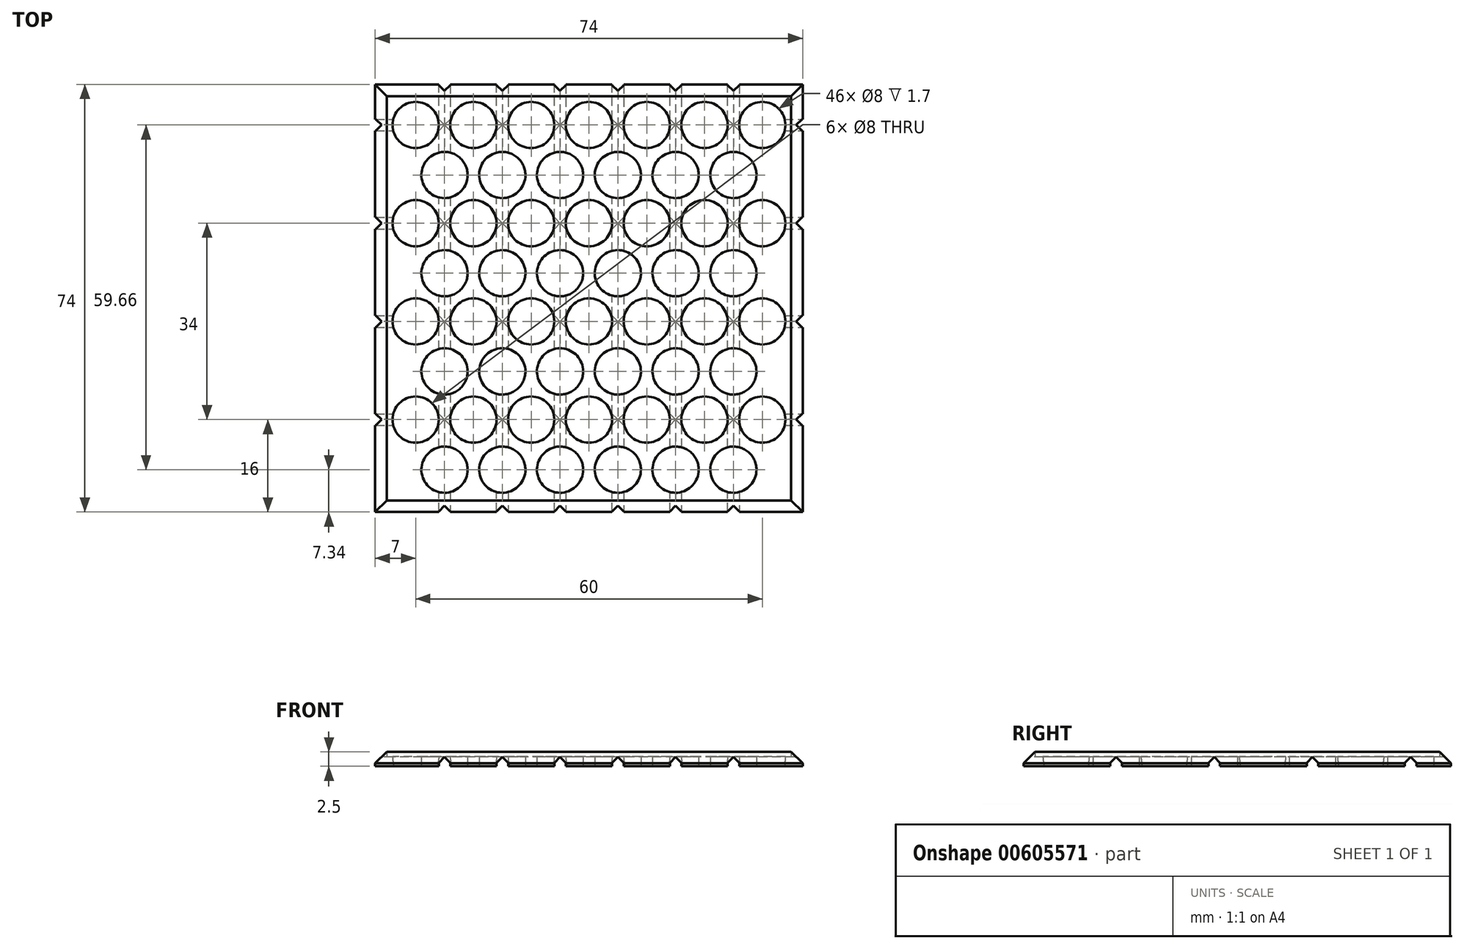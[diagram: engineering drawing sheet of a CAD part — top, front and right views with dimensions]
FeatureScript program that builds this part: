
annotation { "Feature Type Name" : "Feature", "Feature Type Description" : "" }
export const myFeature = defineFeature(function(context is Context, id is Id, definition is map)
    precondition{}
    {
        {
            var Q0;
            Q0=qCreatedBy(makeId("Top.planeOp"),FACE);
            var sketch = newSketch(context, id + "F0", { "sketchPlane" : qUnion([Q0])});
            skLineSegment(sketch, "E0.bottom", {"start": v(0, 0) * mm, "end": v(70, 0) * mm});
            skLineSegment(sketch, "E0.top", {"start": v(0, 70) * mm, "end": v(70, 70) * mm});
            skLineSegment(sketch, "E0.left", {"start": v(0, 0) * mm, "end": v(0, 70) * mm});
            skLineSegment(sketch, "E0.right", {"start": v(70, 0) * mm, "end": v(70, 70) * mm});
            skLineSegment(sketch, "E1.0", {"start": v(-2, 72) * mm, "end": v(72, 72) * mm});
            skLineSegment(sketch, "E1.1", {"start": v(-2, -2) * mm, "end": v(-2, 72) * mm});
            skLineSegment(sketch, "E1.2", {"start": v(-2, -2) * mm, "end": v(72, -2) * mm});
            skLineSegment(sketch, "E1.3", {"start": v(72, -2) * mm, "end": v(72, 72) * mm});
            skSolve(sketch);
        }
        {
            var Q0;
            Q0=makeQuery(id+"F0.imprint","IMPRINT",FACE,{"disambiguationData":[TD([[makeQuery(id+"F0.imprint","IMPRINT",EDGE,{"derivedFrom":sQuery(id+"F0.wireOp",EDGE,"E0.bottom")}),-1.0]])]});
            extrude(context, id + "F1", {"entities" : qUnion([Q0]), "depth" : 2.5 * mm, "offsetDistance" : 25 * mm});
        }
        {
            var Q0;
            Q0=makeQuery(id+"F0.imprint","IMPRINT",FACE,{"disambiguationData":[TD([[makeQuery(id+"F0.imprint","IMPRINT",EDGE,{"derivedFrom":sQuery(id+"F0.wireOp",EDGE,"E0.bottom")}),1.0]])]});
            var Q1;
            Q1=makeQuery(id+"F0.imprint","IMPRINT",FACE,{"disambiguationData":[TD([[makeQuery(id+"F0.imprint","IMPRINT",EDGE,{"derivedFrom":sQuery(id+"F0.wireOp",EDGE,"E0.bottom")}),-1.0]])]});
            extrude(context, id + "F2", {"entities" : qUnion([Q0, Q1]), "operationType" : NewBodyOperationType.ADD, "depth" : 1.7 * mm, "offsetDistance" : 25 * mm});
        }
        {
            var Q0;
            Q0=qCreatedBy(makeId("Top.planeOp"),FACE);
            var sketch = newSketch(context, id + "F3", { "sketchPlane" : qUnion([Q0])});
            skLineSegment(sketch, "E2", {"start": v(9, -4) * mm, "end": v(9, 76) * mm});
            skLineSegment(sketch, "E3", {"start": v(9, 76) * mm, "end": v(11, 76) * mm});
            skLineSegment(sketch, "E4", {"start": v(11, 76) * mm, "end": v(11, -4) * mm});
            skLineSegment(sketch, "E5", {"start": v(11, -4) * mm, "end": v(9, -4) * mm});
            skLineSegment(sketch, "E6.1.0.0", {"start": v(21, -4) * mm, "end": v(19, -4) * mm});
            skLineSegment(sketch, "E6.1.0.1", {"start": v(19, -4) * mm, "end": v(19, 76) * mm});
            skLineSegment(sketch, "E6.1.0.2", {"start": v(21, 76) * mm, "end": v(21, -4) * mm});
            skLineSegment(sketch, "E6.1.0.3", {"start": v(19, 76) * mm, "end": v(21, 76) * mm});
            skLineSegment(sketch, "E6.2.0.0", {"start": v(31, -4) * mm, "end": v(29, -4) * mm});
            skLineSegment(sketch, "E6.2.0.1", {"start": v(29, -4) * mm, "end": v(29, 76) * mm});
            skLineSegment(sketch, "E6.2.0.2", {"start": v(31, 76) * mm, "end": v(31, -4) * mm});
            skLineSegment(sketch, "E6.2.0.3", {"start": v(29, 76) * mm, "end": v(31, 76) * mm});
            skLineSegment(sketch, "E6.3.0.0", {"start": v(41, -4) * mm, "end": v(39, -4) * mm});
            skLineSegment(sketch, "E6.3.0.1", {"start": v(39, -4) * mm, "end": v(39, 76) * mm});
            skLineSegment(sketch, "E6.3.0.2", {"start": v(41, 76) * mm, "end": v(41, -4) * mm});
            skLineSegment(sketch, "E6.3.0.3", {"start": v(39, 76) * mm, "end": v(41, 76) * mm});
            skLineSegment(sketch, "E6.4.0.0", {"start": v(51, -4) * mm, "end": v(49, -4) * mm});
            skLineSegment(sketch, "E6.4.0.1", {"start": v(49, -4) * mm, "end": v(49, 76) * mm});
            skLineSegment(sketch, "E6.4.0.2", {"start": v(51, 76) * mm, "end": v(51, -4) * mm});
            skLineSegment(sketch, "E6.4.0.3", {"start": v(49, 76) * mm, "end": v(51, 76) * mm});
            skLineSegment(sketch, "E6.5.0.0", {"start": v(61, -4) * mm, "end": v(59, -4) * mm});
            skLineSegment(sketch, "E6.5.0.1", {"start": v(59, -4) * mm, "end": v(59, 76) * mm});
            skLineSegment(sketch, "E6.5.0.2", {"start": v(61, 76) * mm, "end": v(61, -4) * mm});
            skLineSegment(sketch, "E6.5.0.3", {"start": v(59, 76) * mm, "end": v(61, 76) * mm});
            skLineSegment(sketch, "E6.direction1", {"start": v(9, -4) * mm, "end": v(19, -4) * mm, "construction": true});
            skSolve(sketch);
        }
        {
            var Q0;
            Q0=qCreatedBy(makeId("Top.planeOp"),FACE);
            var sketch = newSketch(context, id + "F4", { "sketchPlane" : qUnion([Q0])});
            skLineSegment(sketch, "E7.bottom", {"start": v(-4, 13) * mm, "end": v(76, 13) * mm});
            skLineSegment(sketch, "E7.top", {"start": v(-4, 15) * mm, "end": v(76, 15) * mm});
            skLineSegment(sketch, "E7.left", {"start": v(-4, 13) * mm, "end": v(-4, 15) * mm});
            skLineSegment(sketch, "E7.right", {"start": v(76, 13) * mm, "end": v(76, 15) * mm});
            skLineSegment(sketch, "E8.1.0.0", {"start": v(-4, 30) * mm, "end": v(76, 30) * mm});
            skLineSegment(sketch, "E8.1.0.1", {"start": v(-4, 32) * mm, "end": v(76, 32) * mm});
            skLineSegment(sketch, "E8.1.0.2", {"start": v(-4, 30) * mm, "end": v(-4, 32) * mm});
            skLineSegment(sketch, "E8.1.0.3", {"start": v(76, 30) * mm, "end": v(76, 32) * mm});
            skLineSegment(sketch, "E8.2.0.0", {"start": v(-4, 47) * mm, "end": v(76, 47) * mm});
            skLineSegment(sketch, "E8.2.0.1", {"start": v(-4, 49) * mm, "end": v(76, 49) * mm});
            skLineSegment(sketch, "E8.2.0.2", {"start": v(-4, 47) * mm, "end": v(-4, 49) * mm});
            skLineSegment(sketch, "E8.2.0.3", {"start": v(76, 47) * mm, "end": v(76, 49) * mm});
            skLineSegment(sketch, "E8.3.0.0", {"start": v(-4, 64) * mm, "end": v(76, 64) * mm});
            skLineSegment(sketch, "E8.3.0.1", {"start": v(-4, 66) * mm, "end": v(76, 66) * mm});
            skLineSegment(sketch, "E8.3.0.2", {"start": v(-4, 64) * mm, "end": v(-4, 66) * mm});
            skLineSegment(sketch, "E8.3.0.3", {"start": v(76, 64) * mm, "end": v(76, 66) * mm});
            skLineSegment(sketch, "E8.direction1", {"start": v(-4, 13) * mm, "end": v(-4, 30) * mm, "construction": true});
            skSolve(sketch);
        }
        {
            var Q0;
            Q0 = qSketchRegion(id + "F3", true);
            extrude(context, id + "F5", {"entities" : qUnion([Q0]), "operationType" : NewBodyOperationType.REMOVE, "depth" : .6 * mm, "offsetDistance" : 25 * mm});
        }
        {
            var Q0;
            Q0 = qSketchRegion(id + "F4", true);
            extrude(context, id + "F6", {"entities" : qUnion([Q0]), "operationType" : NewBodyOperationType.REMOVE, "depth" : .6 * mm, "offsetDistance" : 25 * mm});
        }
        {
            var Q0;
            Q0=makeQuery(id+"F1.opExtrude","SWEPT_FACE",FACE,{"disambiguationData":[OSD([sQuery(id+"F0.wireOp",EDGE,"E1.2")])]});
            var sketch = newSketch(context, id + "F7", { "sketchPlane" : qUnion([Q0])});
            skLineSegment(sketch, "E9", {"start": v(9, 0.6) * mm, "end": v(10, 1.6) * mm});
            skLineSegment(sketch, "E10", {"start": v(10, 1.6) * mm, "end": v(11, 0.6) * mm});
            skLineSegment(sketch, "E11", {"start": v(11, 0.6) * mm, "end": v(9, 0.6) * mm});
            skLineSegment(sketch, "E12.1.0.0", {"start": v(20, 1.6) * mm, "end": v(21, 0.6) * mm});
            skLineSegment(sketch, "E12.1.0.1", {"start": v(19, 0.6) * mm, "end": v(20, 1.6) * mm});
            skLineSegment(sketch, "E12.1.0.2", {"start": v(21, 0.6) * mm, "end": v(19, 0.6) * mm});
            skLineSegment(sketch, "E12.2.0.0", {"start": v(30, 1.6) * mm, "end": v(31, 0.6) * mm});
            skLineSegment(sketch, "E12.2.0.1", {"start": v(29, 0.6) * mm, "end": v(30, 1.6) * mm});
            skLineSegment(sketch, "E12.2.0.2", {"start": v(31, 0.6) * mm, "end": v(29, 0.6) * mm});
            skLineSegment(sketch, "E12.3.0.0", {"start": v(40, 1.6) * mm, "end": v(41, 0.6) * mm});
            skLineSegment(sketch, "E12.3.0.1", {"start": v(39, 0.6) * mm, "end": v(40, 1.6) * mm});
            skLineSegment(sketch, "E12.3.0.2", {"start": v(41, 0.6) * mm, "end": v(39, 0.6) * mm});
            skLineSegment(sketch, "E12.4.0.0", {"start": v(50, 1.6) * mm, "end": v(51, 0.6) * mm});
            skLineSegment(sketch, "E12.4.0.1", {"start": v(49, 0.6) * mm, "end": v(50, 1.6) * mm});
            skLineSegment(sketch, "E12.4.0.2", {"start": v(51, 0.6) * mm, "end": v(49, 0.6) * mm});
            skLineSegment(sketch, "E12.5.0.0", {"start": v(60, 1.6) * mm, "end": v(61, 0.6) * mm});
            skLineSegment(sketch, "E12.5.0.1", {"start": v(59, 0.6) * mm, "end": v(60, 1.6) * mm});
            skLineSegment(sketch, "E12.5.0.2", {"start": v(61, 0.6) * mm, "end": v(59, 0.6) * mm});
            skLineSegment(sketch, "E12.direction1", {"start": v(9, 0.6) * mm, "end": v(19, 0.6) * mm, "construction": true});
            skSolve(sketch);
        }
        {
            var Q0;
            Q0 = qSketchRegion(id + "F7", true);
            var Q1;
            Q1=makeQuery(id+"F1.opExtrude","SWEPT_FACE",FACE,{"disambiguationData":[OSD([sQuery(id+"F0.wireOp",EDGE,"E1.0")])]});
            extrude(context, id + "F8", {"entities" : qUnion([Q0]), "operationType" : NewBodyOperationType.REMOVE, "endBound" : BoundingType.UP_TO_NEXT, "oppositeDirection" : true, "depth" : 80 * mm, "endBoundEntityFace" : qUnion([Q1]), "offsetDistance" : 25 * mm});
        }
        {
            var Q0;
            Q0=makeQuery(id+"F1.opExtrude","SWEPT_FACE",FACE,{"disambiguationData":[OSD([sQuery(id+"F0.wireOp",EDGE,"E1.1")])]});
            var sketch = newSketch(context, id + "F9", { "sketchPlane" : qUnion([Q0])});
            skLineSegment(sketch, "E13", {"start": v(-66, 0.6) * mm, "end": v(-65, 1.6) * mm});
            skLineSegment(sketch, "E14", {"start": v(-65, 1.6) * mm, "end": v(-64, 0.6) * mm});
            skLineSegment(sketch, "E15", {"start": v(-64, 0.6) * mm, "end": v(-66, 0.6) * mm});
            skLineSegment(sketch, "E16.1.0.0", {"start": v(-48, 1.6) * mm, "end": v(-47, 0.6) * mm});
            skLineSegment(sketch, "E16.1.0.1", {"start": v(-49, 0.6) * mm, "end": v(-48, 1.6) * mm});
            skLineSegment(sketch, "E16.1.0.2", {"start": v(-47, 0.6) * mm, "end": v(-49, 0.6) * mm});
            skLineSegment(sketch, "E16.2.0.0", {"start": v(-31, 1.6) * mm, "end": v(-30, 0.6) * mm});
            skLineSegment(sketch, "E16.2.0.1", {"start": v(-32, 0.6) * mm, "end": v(-31, 1.6) * mm});
            skLineSegment(sketch, "E16.2.0.2", {"start": v(-30, 0.6) * mm, "end": v(-32, 0.6) * mm});
            skLineSegment(sketch, "E16.3.0.0", {"start": v(-14, 1.6) * mm, "end": v(-13, 0.6) * mm});
            skLineSegment(sketch, "E16.3.0.1", {"start": v(-15, 0.6) * mm, "end": v(-14, 1.6) * mm});
            skLineSegment(sketch, "E16.3.0.2", {"start": v(-13, 0.6) * mm, "end": v(-15, 0.6) * mm});
            skLineSegment(sketch, "E16.direction1", {"start": v(-66, 0.6) * mm, "end": v(-49, 0.6) * mm, "construction": true});
            skSolve(sketch);
        }
        {
            var Q0;
            Q0 = qSketchRegion(id + "F9", true);
            extrude(context, id + "F10", {"entities" : qUnion([Q0]), "operationType" : NewBodyOperationType.REMOVE, "endBound" : BoundingType.THROUGH_ALL, "oppositeDirection" : true, "depth" : 25 * mm, "offsetDistance" : 25 * mm});
        }
        {
            var Q0;
            Q0=makeQuery(id+"F0.imprint","IMPRINT",FACE,{"disambiguationData":[TD([[makeQuery(id+"F0.imprint","IMPRINT",EDGE,{"derivedFrom":sQuery(id+"F0.wireOp",EDGE,"E0.bottom")}),1.0]])]});
            var sketch = newSketch(context, id + "F11", { "sketchPlane" : qUnion([Q0])});
            skCircle(sketch, "E17", {"center": v(5, 65) * mm, "radius": 4 * mm});
            skCircle(sketch, "E18.1.0.0", {"center": v(15, 65) * mm, "radius": 4 * mm});
            skCircle(sketch, "E18.2.0.0", {"center": v(25, 65) * mm, "radius": 4 * mm});
            skCircle(sketch, "E18.3.0.0", {"center": v(35, 65) * mm, "radius": 4 * mm});
            skCircle(sketch, "E18.4.0.0", {"center": v(45, 65) * mm, "radius": 4 * mm});
            skLineSegment(sketch, "E18.direction1", {"start": v(5, 65) * mm, "end": v(15, 65) * mm, "construction": true});
            skCircle(sketch, "E19", {"center": v(10, 56.34) * mm, "radius": 4 * mm});
            skLineSegment(sketch, "E20", {"start": v(5, 65) * mm, "end": v(10, 56.34) * mm, "construction": true});
            skLineSegment(sketch, "E21", {"start": v(10, 56.34) * mm, "end": v(15, 65) * mm, "construction": true});
            skCircle(sketch, "E22.1.0.0", {"center": v(20, 56.34) * mm, "radius": 4 * mm});
            skCircle(sketch, "E22.2.0.0", {"center": v(30, 56.34) * mm, "radius": 4 * mm});
            skCircle(sketch, "E22.3.0.0", {"center": v(40, 56.34) * mm, "radius": 4 * mm});
            skLineSegment(sketch, "E22.direction1", {"start": v(10, 56.34) * mm, "end": v(20, 56.34) * mm, "construction": true});
            skCircle(sketch, "E23.0.5.0", {"center": v(55, 65) * mm, "radius": 4 * mm});
            skCircle(sketch, "E23.0.6.0", {"center": v(65, 65) * mm, "radius": 4 * mm});
            skCircle(sketch, "E24.0.4.0", {"center": v(50, 56.34) * mm, "radius": 4 * mm});
            skCircle(sketch, "E24.0.5.0", {"center": v(60, 56.34) * mm, "radius": 4 * mm});
            skCircle(sketch, "E25.1.0.0", {"center": v(55, 48) * mm, "radius": 4 * mm});
            skCircle(sketch, "E25.1.0.1", {"center": v(20, 39.34) * mm, "radius": 4 * mm});
            skCircle(sketch, "E25.1.0.2", {"center": v(65, 48) * mm, "radius": 4 * mm});
            skCircle(sketch, "E25.1.0.3", {"center": v(60, 39.34) * mm, "radius": 4 * mm});
            skCircle(sketch, "E25.1.0.4", {"center": v(50, 39.34) * mm, "radius": 4 * mm});
            skCircle(sketch, "E25.1.0.5", {"center": v(30, 39.34) * mm, "radius": 4 * mm});
            skCircle(sketch, "E25.1.0.6", {"center": v(10, 39.34) * mm, "radius": 4 * mm});
            skCircle(sketch, "E25.1.0.7", {"center": v(5, 48) * mm, "radius": 4 * mm});
            skCircle(sketch, "E25.1.0.8", {"center": v(40, 39.34) * mm, "radius": 4 * mm});
            skCircle(sketch, "E25.1.0.9", {"center": v(15, 48) * mm, "radius": 4 * mm});
            skCircle(sketch, "E25.1.0.10", {"center": v(25, 48) * mm, "radius": 4 * mm});
            skCircle(sketch, "E25.1.0.11", {"center": v(35, 48) * mm, "radius": 4 * mm});
            skCircle(sketch, "E25.1.0.12", {"center": v(45, 48) * mm, "radius": 4 * mm});
            skCircle(sketch, "E25.2.0.0", {"center": v(55, 31) * mm, "radius": 4 * mm});
            skCircle(sketch, "E25.2.0.1", {"center": v(20, 22.34) * mm, "radius": 4 * mm});
            skCircle(sketch, "E25.2.0.2", {"center": v(65, 31) * mm, "radius": 4 * mm});
            skCircle(sketch, "E25.2.0.3", {"center": v(60, 22.34) * mm, "radius": 4 * mm});
            skCircle(sketch, "E25.2.0.4", {"center": v(50, 22.34) * mm, "radius": 4 * mm});
            skCircle(sketch, "E25.2.0.5", {"center": v(30, 22.34) * mm, "radius": 4 * mm});
            skCircle(sketch, "E25.2.0.6", {"center": v(10, 22.34) * mm, "radius": 4 * mm});
            skCircle(sketch, "E25.2.0.7", {"center": v(5, 31) * mm, "radius": 4 * mm});
            skCircle(sketch, "E25.2.0.8", {"center": v(40, 22.34) * mm, "radius": 4 * mm});
            skCircle(sketch, "E25.2.0.9", {"center": v(15, 31) * mm, "radius": 4 * mm});
            skCircle(sketch, "E25.2.0.10", {"center": v(25, 31) * mm, "radius": 4 * mm});
            skCircle(sketch, "E25.2.0.11", {"center": v(35, 31) * mm, "radius": 4 * mm});
            skCircle(sketch, "E25.2.0.12", {"center": v(45, 31) * mm, "radius": 4 * mm});
            skCircle(sketch, "E25.3.0.0", {"center": v(55, 14) * mm, "radius": 4 * mm});
            skCircle(sketch, "E25.3.0.1", {"center": v(20, 5.34) * mm, "radius": 4 * mm});
            skCircle(sketch, "E25.3.0.2", {"center": v(65, 14) * mm, "radius": 4 * mm});
            skCircle(sketch, "E25.3.0.3", {"center": v(60, 5.34) * mm, "radius": 4 * mm});
            skCircle(sketch, "E25.3.0.4", {"center": v(50, 5.34) * mm, "radius": 4 * mm});
            skCircle(sketch, "E25.3.0.5", {"center": v(30, 5.34) * mm, "radius": 4 * mm});
            skCircle(sketch, "E25.3.0.6", {"center": v(10, 5.34) * mm, "radius": 4 * mm});
            skCircle(sketch, "E25.3.0.7", {"center": v(5, 14) * mm, "radius": 4 * mm});
            skCircle(sketch, "E25.3.0.8", {"center": v(40, 5.34) * mm, "radius": 4 * mm});
            skCircle(sketch, "E25.3.0.9", {"center": v(15, 14) * mm, "radius": 4 * mm});
            skCircle(sketch, "E25.3.0.10", {"center": v(25, 14) * mm, "radius": 4 * mm});
            skCircle(sketch, "E25.3.0.11", {"center": v(35, 14) * mm, "radius": 4 * mm});
            skCircle(sketch, "E25.3.0.12", {"center": v(45, 14) * mm, "radius": 4 * mm});
            skLineSegment(sketch, "E25.direction1", {"start": v(10, 56.34) * mm, "end": v(10, 39.34) * mm, "construction": true});
            skSolve(sketch);
        }
        {
            var Q0;
            Q0=makeQuery(id+"F1.opExtrude","CAP_EDGE",EDGE,{"disambiguationData":[OSD([sQuery(id+"F0.wireOp",EDGE,"E1.3")])],"isStart":false});
            var Q1;
            Q1=makeQuery(id+"F1.opExtrude","CAP_EDGE",EDGE,{"disambiguationData":[OSD([sQuery(id+"F0.wireOp",EDGE,"E1.2")])],"isStart":false});
            var Q2;
            Q2=makeQuery(id+"F1.opExtrude","CAP_EDGE",EDGE,{"disambiguationData":[OSD([sQuery(id+"F0.wireOp",EDGE,"E1.0")])],"isStart":false});
            var Q3;
            Q3=makeQuery(id+"F1.opExtrude","CAP_EDGE",EDGE,{"disambiguationData":[OSD([sQuery(id+"F0.wireOp",EDGE,"E1.1")])],"isStart":false});
            chamfer(context, id + "F12", {"entities" : qUnion([Q0, Q1, Q2, Q3]), "width" : 2 * mm, "tangentPropagation" : true});
        }
        {
            var Q0;
            Q0 = qSketchRegion(id + "F11", true);
            extrude(context, id + "F13", {"entities" : qUnion([Q0]), "operationType" : NewBodyOperationType.REMOVE, "endBound" : BoundingType.THROUGH_ALL, "depth" : 25 * mm, "offsetDistance" : 25 * mm});
        }
    });
